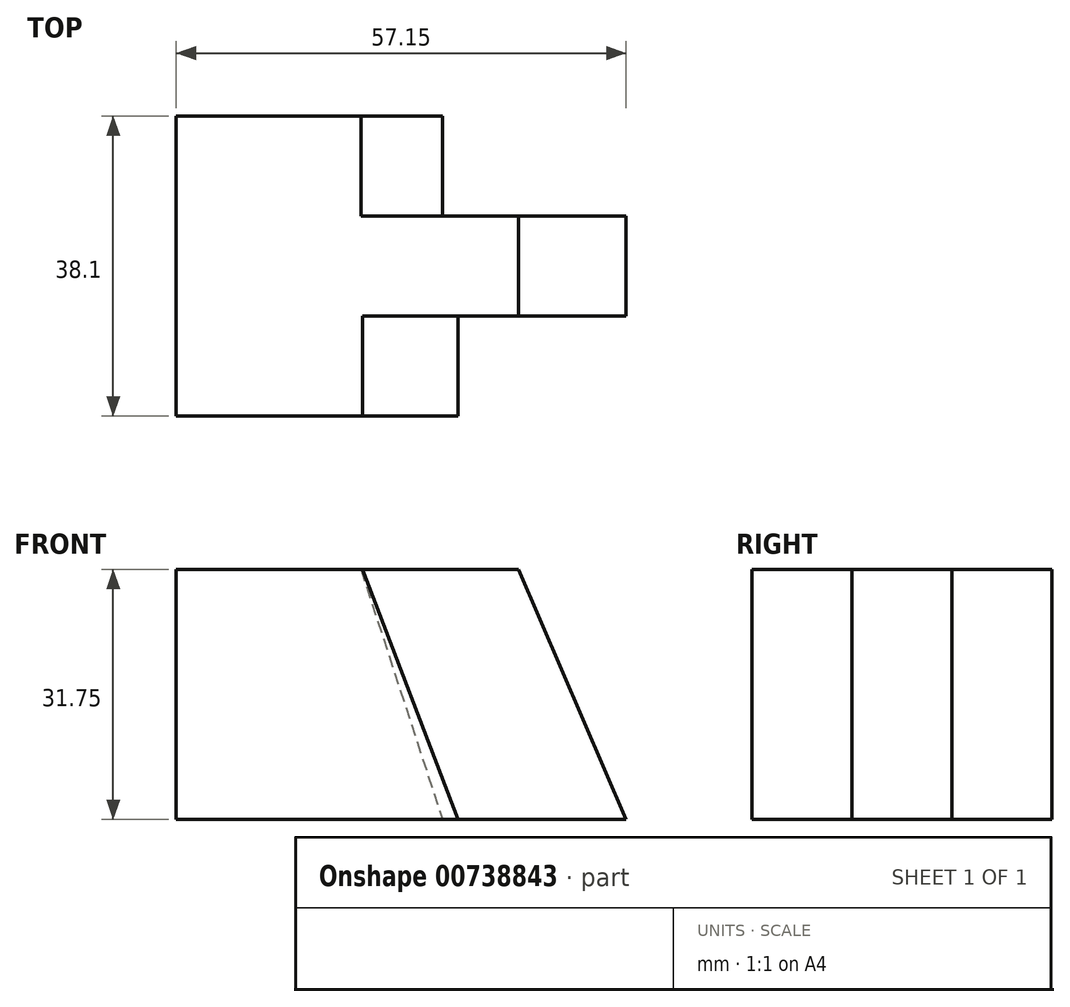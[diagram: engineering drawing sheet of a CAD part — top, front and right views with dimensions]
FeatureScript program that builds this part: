
annotation { "Feature Type Name" : "Feature", "Feature Type Description" : "" }
export const myFeature = defineFeature(function(context is Context, id is Id, definition is map)
    precondition{}
    {
        {
            var Q0;
            Q0=qCreatedBy(makeId("Front.planeOp"),FACE);
            var sketch = newSketch(context, id + "F0", { "sketchPlane" : qUnion([Q0])});
            skLineSegment(sketch, "E0", {"start": v(0, 0) * mm, "end": v(57.15, 0) * mm});
            skLineSegment(sketch, "E1", {"start": v(57.15, 0) * mm, "end": v(57.15, 31.75) * mm});
            skLineSegment(sketch, "E2", {"start": v(57.15, 31.75) * mm, "end": v(0, 31.75) * mm});
            skLineSegment(sketch, "E3", {"start": v(0, 31.75) * mm, "end": v(0, 0) * mm});
            skSolve(sketch);
        }
        {
            var Q0;
            Q0=makeQuery(id+"F0.imprint","IMPRINT",FACE,{"disambiguationData":[TD([[makeQuery(id+"F0.imprint","IMPRINT",EDGE,{"derivedFrom":sQuery(id+"F0.wireOp",EDGE,"E0")}),1.0]])]});
            extrude(context, id + "F1", {"entities" : qUnion([Q0]), "depth" : 38.1 * mm, "offsetDistance" : 25.4 * mm});
        }
        {
            var Q0;
            Q0=makeQuery(id+"F1.opExtrude","CAP_FACE",FACE,{"disambiguationData":[OSD([sQuery(id+"F0.wireOp",EDGE,"E0"),sQuery(id+"F0.wireOp",EDGE,"E1"),sQuery(id+"F0.wireOp",EDGE,"E2"),sQuery(id+"F0.wireOp",EDGE,"E3")])],"isStart":false});
            extrude(context, id + "F2", {"entities" : qUnion([Q0]), "operationType" : NewBodyOperationType.ADD, "depth" : 12.7 * mm, "offsetDistance" : 25.4 * mm});
        }
        {
            var Q0;
            Q0=makeQuery(id+"F2.opExtrude","CAP_FACE",FACE,{"disambiguationData":[OSD([sQuery(id+"F0.wireOp",EDGE,"E0"),sQuery(id+"F0.wireOp",EDGE,"E1"),sQuery(id+"F0.wireOp",EDGE,"E2"),sQuery(id+"F0.wireOp",EDGE,"E3")])],"isStart":false});
            var sketch = newSketch(context, id + "F3", { "sketchPlane" : qUnion([Q0])});
            skLineSegment(sketch, "E4", {"start": v(23.68, 31.75) * mm, "end": v(35.82, 0) * mm});
            skSolve(sketch);
        }
        {
            var Q0;
            {var subQ0=sQuery(id+"F3.wireOp",EDGE,"E4");Q0=makeQuery(id+"F3.imprint","IMPRINT",FACE,{"disambiguationData":[TD([[makeQuery(id+"F3.imprint","IMPRINT",EDGE,{"derivedFrom":subQ0}),1.0]])]});}
            extrude(context, id + "F4", {"entities" : qUnion([Q0]), "operationType" : NewBodyOperationType.REMOVE, "oppositeDirection" : true, "depth" : 12.7 * mm, "offsetDistance" : 25.4 * mm});
        }
        {
            var Q0;
            Q0=makeQuery(id+"F1.opExtrude","CAP_FACE",FACE,{"disambiguationData":[OSD([sQuery(id+"F0.wireOp",EDGE,"E0"),sQuery(id+"F0.wireOp",EDGE,"E1"),sQuery(id+"F0.wireOp",EDGE,"E2"),sQuery(id+"F0.wireOp",EDGE,"E3")])],"isStart":true});
            var sketch = newSketch(context, id + "F5", { "sketchPlane" : qUnion([Q0])});
            skLineSegment(sketch, "E5", {"start": v(-23.45, 31.75) * mm, "end": v(-33.82, 0) * mm});
            skSolve(sketch);
        }
        {
            var Q0;
            {var subQ0=sQuery(id+"F5.wireOp",EDGE,"E5");Q0=makeQuery(id+"F5.imprint","IMPRINT",FACE,{"disambiguationData":[TD([[makeQuery(id+"F5.imprint","IMPRINT",EDGE,{"derivedFrom":subQ0}),-1.0]])]});}
            extrude(context, id + "F6", {"entities" : qUnion([Q0]), "operationType" : NewBodyOperationType.REMOVE, "oppositeDirection" : true, "depth" : 12.7 * mm, "offsetDistance" : 25.4 * mm});
        }
        {
            var Q0;
            Q0=makeQuery(id+"F4.boolean.opBoolean","COPY",FACE,{"derivedFrom":makeQuery(id+"F4.opExtrude","CAP_FACE",FACE,{"disambiguationData":[OSD([sQuery(id+"F0.wireOp",EDGE,"E0"),sQuery(id+"F0.wireOp",EDGE,"E1"),sQuery(id+"F0.wireOp",EDGE,"E2"),sQuery(id+"F3.wireOp",EDGE,"E4")])],"isStart":false})});
            var sketch = newSketch(context, id + "F7", { "sketchPlane" : qUnion([Q0])});
            skLineSegment(sketch, "E6", {"start": v(43.5, 31.75) * mm, "end": v(57.15, 0) * mm});
            skSolve(sketch);
        }
        {
            var Q0;
            {var subQ0=sQuery(id+"F7.wireOp",EDGE,"E6");Q0=makeQuery(id+"F7.imprint","IMPRINT",FACE,{"disambiguationData":[TD([[makeQuery(id+"F7.imprint","IMPRINT",EDGE,{"derivedFrom":subQ0}),1.0]])]});}
            extrude(context, id + "F8", {"entities" : qUnion([Q0]), "operationType" : NewBodyOperationType.REMOVE, "endBound" : BoundingType.THROUGH_ALL, "oppositeDirection" : true, "depth" : 25.4 * mm, "offsetDistance" : 25.4 * mm});
        }
        {
            var Q0;
            Q0=makeQuery(id+"F4.boolean.opBoolean","COPY",FACE,{"derivedFrom":makeQuery(id+"F4.opExtrude","CAP_FACE",FACE,{"disambiguationData":[OSD([sQuery(id+"F0.wireOp",EDGE,"E0"),sQuery(id+"F0.wireOp",EDGE,"E1"),sQuery(id+"F0.wireOp",EDGE,"E2"),sQuery(id+"F3.wireOp",EDGE,"E4")])],"isStart":false})});
            extrude(context, id + "F9", {"entities" : qUnion([Q0]), "operationType" : NewBodyOperationType.REMOVE, "oppositeDirection" : true, "depth" : 6.35 * mm, "offsetDistance" : 25.4 * mm});
        }
        {
            var Q0;
            Q0=makeQuery(id+"F6.boolean.opBoolean","COPY",FACE,{"derivedFrom":makeQuery(id+"F6.opExtrude","CAP_FACE",FACE,{"disambiguationData":[OSD([sQuery(id+"F0.wireOp",EDGE,"E0"),sQuery(id+"F0.wireOp",EDGE,"E1"),sQuery(id+"F0.wireOp",EDGE,"E2"),sQuery(id+"F5.wireOp",EDGE,"E5")])],"isStart":false})});
            extrude(context, id + "F10", {"entities" : qUnion([Q0]), "operationType" : NewBodyOperationType.REMOVE, "oppositeDirection" : true, "depth" : 6.35 * mm, "offsetDistance" : 25.4 * mm});
        }
        {
            var Q0;
            Q0=makeQuery(id+"F1.opExtrude","CAP_FACE",FACE,{"disambiguationData":[OSD([sQuery(id+"F0.wireOp",EDGE,"E0"),sQuery(id+"F0.wireOp",EDGE,"E1"),sQuery(id+"F0.wireOp",EDGE,"E2"),sQuery(id+"F0.wireOp",EDGE,"E3")])],"isStart":true});
            extrude(context, id + "F11", {"entities" : qUnion([Q0]), "operationType" : NewBodyOperationType.REMOVE, "oppositeDirection" : true, "depth" : 6.35 * mm, "offsetDistance" : 25.4 * mm});
        }
        {
            var Q0;
            Q0=makeQuery(id+"F2.opExtrude","CAP_FACE",FACE,{"disambiguationData":[OSD([sQuery(id+"F0.wireOp",EDGE,"E0"),sQuery(id+"F0.wireOp",EDGE,"E1"),sQuery(id+"F0.wireOp",EDGE,"E2"),sQuery(id+"F0.wireOp",EDGE,"E3")])],"isStart":false});
            extrude(context, id + "F12", {"entities" : qUnion([Q0]), "operationType" : NewBodyOperationType.REMOVE, "oppositeDirection" : true, "depth" : 6.35 * mm, "offsetDistance" : 25.4 * mm});
        }
    });
